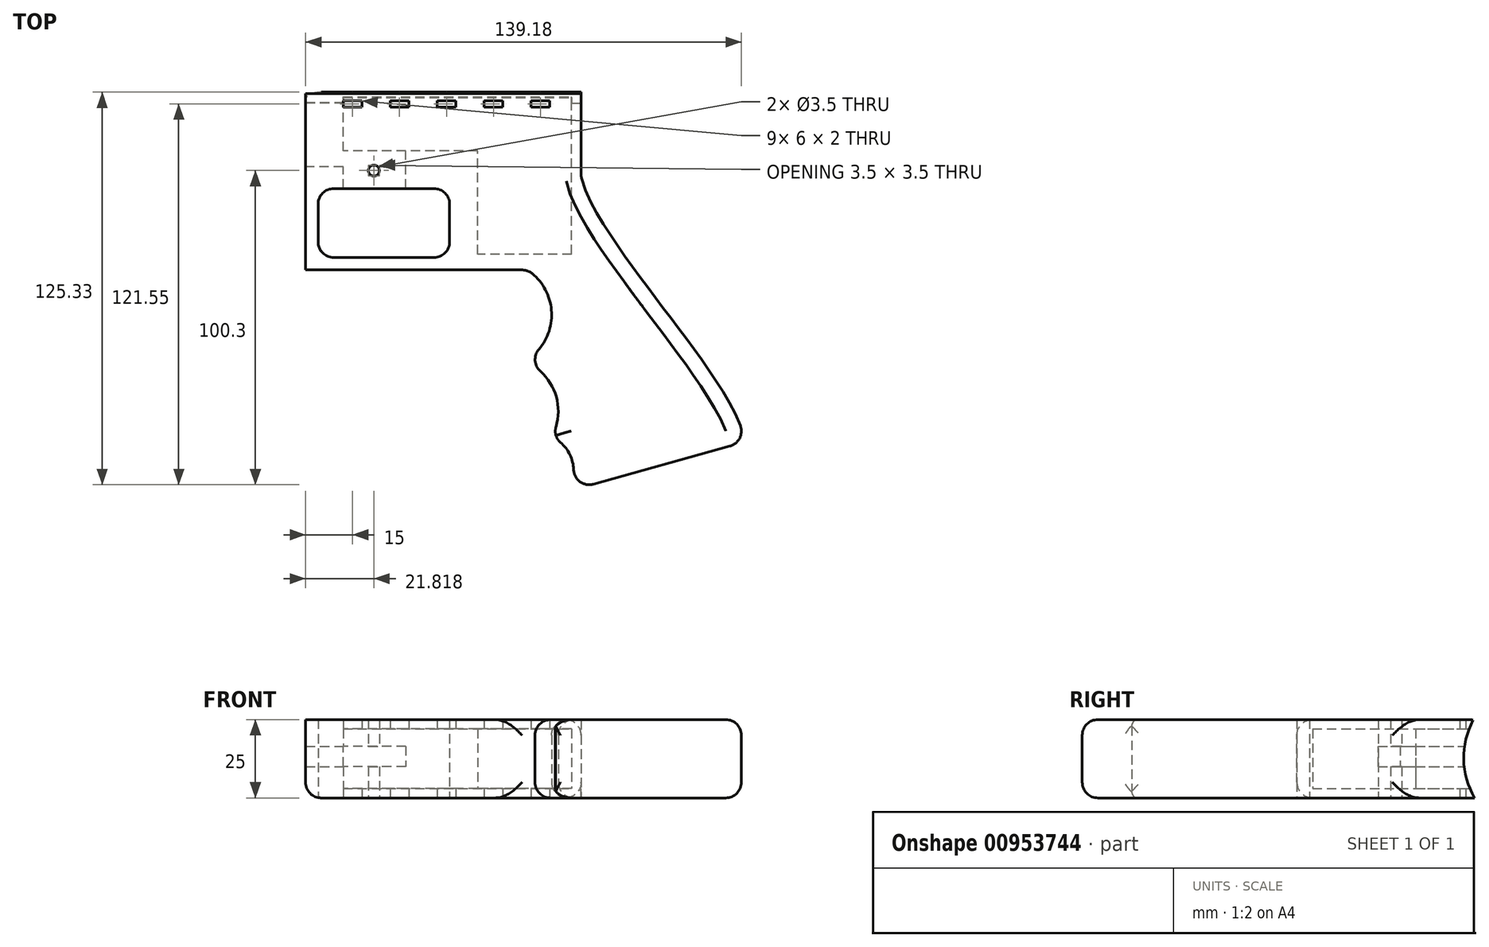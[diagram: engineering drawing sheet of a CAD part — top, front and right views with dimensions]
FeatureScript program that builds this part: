
annotation { "Feature Type Name" : "Feature", "Feature Type Description" : "" }
export const myFeature = defineFeature(function(context is Context, id is Id, definition is map)
    precondition{}
    {
        {
            var Q0;
            Q0=qCreatedBy(makeId("Top.planeOp"),FACE);
            var sketch = newSketch(context, id + "F0", { "sketchPlane" : qUnion([Q0])});
            skLineSegment(sketch, "E0.bottom", {"start": v(44, -30) * mm, "end": v(-44, -30) * mm});
            skLineSegment(sketch, "E0.top", {"start": v(44, 30) * mm, "end": v(-44, 30) * mm});
            skLineSegment(sketch, "E0.left", {"start": v(44, -30) * mm, "end": v(44, 30) * mm});
            skLineSegment(sketch, "E0.right", {"start": v(-44, -30) * mm, "end": v(-44, 30) * mm});
            skPoint(sketch, "E0.middle", {"position": v(0, 0) * mm});
            skLineSegment(sketch, "E1.bottom", {"start": v(-40, -26) * mm, "end": v(2, -26) * mm});
            skLineSegment(sketch, "E1.top", {"start": v(-40, -4) * mm, "end": v(2, -4) * mm});
            skLineSegment(sketch, "E1.left", {"start": v(-40, -26) * mm, "end": v(-40, -4) * mm});
            skLineSegment(sketch, "E1.right", {"start": v(2, -26) * mm, "end": v(2, -4) * mm});
            skLineSegment(sketch, "E2.bottom", {"start": v(-32, 24) * mm, "end": v(-26, 24) * mm});
            skLineSegment(sketch, "E2.top", {"start": v(-32, 22) * mm, "end": v(-26, 22) * mm});
            skLineSegment(sketch, "E2.left", {"start": v(-32, 24) * mm, "end": v(-32, 22) * mm});
            skLineSegment(sketch, "E2.right", {"start": v(-26, 24) * mm, "end": v(-26, 22) * mm});
            skLineSegment(sketch, "E3.1.0.0", {"start": v(-17, 22) * mm, "end": v(-11, 22) * mm});
            skLineSegment(sketch, "E3.1.0.1", {"start": v(-17, 24) * mm, "end": v(-17, 22) * mm});
            skLineSegment(sketch, "E3.1.0.2", {"start": v(-17, 24) * mm, "end": v(-11, 24) * mm});
            skLineSegment(sketch, "E3.1.0.3", {"start": v(-11, 24) * mm, "end": v(-11, 22) * mm});
            skLineSegment(sketch, "E3.2.0.0", {"start": v(-2, 22) * mm, "end": v(4, 22) * mm});
            skLineSegment(sketch, "E3.2.0.1", {"start": v(-2, 24) * mm, "end": v(-2, 22) * mm});
            skLineSegment(sketch, "E3.2.0.2", {"start": v(-2, 24) * mm, "end": v(4, 24) * mm});
            skLineSegment(sketch, "E3.2.0.3", {"start": v(4, 24) * mm, "end": v(4, 22) * mm});
            skLineSegment(sketch, "E3.3.0.0", {"start": v(13, 22) * mm, "end": v(19, 22) * mm});
            skLineSegment(sketch, "E3.3.0.1", {"start": v(13, 24) * mm, "end": v(13, 22) * mm});
            skLineSegment(sketch, "E3.3.0.2", {"start": v(13, 24) * mm, "end": v(19, 24) * mm});
            skLineSegment(sketch, "E3.3.0.3", {"start": v(19, 24) * mm, "end": v(19, 22) * mm});
            skLineSegment(sketch, "E3.4.0.0", {"start": v(28, 22) * mm, "end": v(34, 22) * mm});
            skLineSegment(sketch, "E3.4.0.1", {"start": v(28, 24) * mm, "end": v(28, 22) * mm});
            skLineSegment(sketch, "E3.4.0.2", {"start": v(28, 24) * mm, "end": v(34, 24) * mm});
            skLineSegment(sketch, "E3.4.0.3", {"start": v(34, 24) * mm, "end": v(34, 22) * mm});
            skLineSegment(sketch, "E3.direction1", {"start": v(-32, 22) * mm, "end": v(-17, 22) * mm, "construction": true});
            skPoint(sketch, "E4", {"position": v(44, 0) * mm});
            skFitSpline(sketch, "E5", {"points": [v(44, 0) * mm, v(96, -85) * mm], "startDerivative": vector(11.02, -60.11) * mm, "endDerivative": vector(0.72, -52.1) * mm});
            skLineSegment(sketch, "E6", {"start": v(96, -85) * mm, "end": v(42.05, -100) * mm});
            skLineSegment(sketch, "E7", {"start": v(42.05, -100) * mm, "end": v(41.24, -97.1) * mm});
            skArc(sketch, "E8", {"start": v(41.24, -97.1) * mm, "mid": v(40.82, -89.9) * mm, "end": v(36.33, -84.24) * mm});
            skLineSegment(sketch, "E9", {"start": v(36.33, -84.24) * mm, "end": v(35.52, -81.35) * mm});
            skArc(sketch, "E10", {"start": v(35.52, -81.35) * mm, "mid": v(35.86, -69.78) * mm, "end": v(28.72, -60.68) * mm});
            skLineSegment(sketch, "E11", {"start": v(28.72, -60.68) * mm, "end": v(27.92, -57.8) * mm});
            skArc(sketch, "E12", {"start": v(27.92, -57.8) * mm, "mid": v(34.57, -43.6) * mm, "end": v(26.78, -30) * mm});
            skSolve(sketch);
        }
        {
            var Q0;
            {var subQ4=sQuery(id+"F0.wireOp",EDGE,"E0.top");Q0=makeQuery(id+"F0.imprint","IMPRINT",FACE,{"disambiguationData":[TD([[makeQuery(id+"F0.imprint","IMPRINT",EDGE,{"derivedFrom":subQ4}),1.0]])]});}
            var Q1;
            {var subQ3=sQuery(id+"F0.wireOp",EDGE,"E5");Q1=makeQuery(id+"F0.imprint","IMPRINT",FACE,{"disambiguationData":[TD([[makeQuery(id+"F0.imprint","IMPRINT",EDGE,{"derivedFrom":subQ3}),-1.0]])]});}
            extrude(context, id + "F1", {"entities" : qUnion([Q0, Q1]), "depth" : 25 * mm, "offsetDistance" : 25 * mm});
        }
        {
            var Q0;
            Q0=makeQuery(id+"F1.opExtrude","SWEPT_FACE",FACE,{"disambiguationData":[OSD([sQuery(id+"F0.wireOp",EDGE,"E0.top")])]});
            var sketch = newSketch(context, id + "F2", { "sketchPlane" : qUnion([Q0])});
            skLineSegment(sketch, "E13.bottom", {"start": v(-41, 22) * mm, "end": v(32, 22) * mm});
            skLineSegment(sketch, "E13.top", {"start": v(-41, 3) * mm, "end": v(32, 3) * mm});
            skLineSegment(sketch, "E13.left", {"start": v(-41, 22) * mm, "end": v(-41, 3) * mm});
            skLineSegment(sketch, "E13.right", {"start": v(32, 22) * mm, "end": v(32, 3) * mm});
            skPoint(sketch, "E14", {"position": v(-41, 3) * mm});
            skPoint(sketch, "E15", {"position": v(-41, 22) * mm});
            skPoint(sketch, "E16", {"position": v(32, 3) * mm});
            skLineSegment(sketch, "E17", {"start": v(-11, 22) * mm, "end": v(-11, 3) * mm});
            skLineSegment(sketch, "E18.bottom", {"start": v(12, 16.48) * mm, "end": v(44, 16.48) * mm});
            skLineSegment(sketch, "E18.top", {"start": v(12, 9.98) * mm, "end": v(44, 9.98) * mm});
            skLineSegment(sketch, "E18.left", {"start": v(12, 16.48) * mm, "end": v(12, 9.98) * mm});
            skLineSegment(sketch, "E18.right", {"start": v(44, 16.48) * mm, "end": v(44, 9.98) * mm});
            skSolve(sketch);
        }
        {
            var Q0;
            Q0 = qSketchRegion(id + "F2", true);
            extrude(context, id + "F3", {"entities" : qUnion([Q0]), "operationType" : NewBodyOperationType.REMOVE, "oppositeDirection" : true, "depth" : 22 * mm, "offsetDistance" : 25 * mm});
        }
        {
            var Q0;
            {var subQ0=sQuery(id+"F2.wireOp",EDGE,"E13.left");Q0=makeQuery(id+"F2.imprint","IMPRINT",FACE,{"disambiguationData":[TD([[makeQuery(id+"F2.imprint","IMPRINT",EDGE,{"derivedFrom":subQ0}),1.0]])]});}
            extrude(context, id + "F4", {"entities" : qUnion([Q0]), "operationType" : NewBodyOperationType.REMOVE, "oppositeDirection" : true, "depth" : 55 * mm, "offsetDistance" : 25 * mm});
        }
        {
            var Q0;
            {var subQ5=sQuery(id+"F2.wireOp",EDGE,"E18.left");Q0=makeQuery(id+"F2.imprint","IMPRINT",FACE,{"disambiguationData":[TD([[makeQuery(id+"F2.imprint","IMPRINT",EDGE,{"derivedFrom":subQ5}),1.0]])]});}
            var Q1;
            Q1=makeQuery(id+"F1.opExtrude","SWEPT_FACE",FACE,{"disambiguationData":[OSD([sQuery(id+"F0.wireOp",EDGE,"E1.top")])]});
            extrude(context, id + "F5", {"entities" : qUnion([Q0]), "operationType" : NewBodyOperationType.REMOVE, "endBound" : BoundingType.UP_TO_SURFACE, "oppositeDirection" : true, "depth" : 25 * mm, "endBoundEntityFace" : qUnion([Q1]), "offsetDistance" : 25 * mm});
        }
        {
            var Q0;
            {var subQ5=sQuery(id+"F2.wireOp",EDGE,"E18.right");Q0=makeQuery(id+"F2.imprint","IMPRINT",FACE,{"disambiguationData":[TD([[makeQuery(id+"F2.imprint","IMPRINT",EDGE,{"derivedFrom":subQ5}),-1.0]])]});}
            extrude(context, id + "F6", {"entities" : qUnion([Q0]), "operationType" : NewBodyOperationType.REMOVE, "oppositeDirection" : true, "depth" : 27 * mm, "offsetDistance" : 25 * mm});
        }
        {
            var Q0;
            Q0=makeQuery(id+"F1.opExtrude","SWEPT_FACE",FACE,{"disambiguationData":[OSD([sQuery(id+"F0.wireOp",EDGE,"E12")])]});
            fillet(context, id + "F7", {"entities" : qUnion([Q0]), "radius" : 5 * mm, "tangentPropagation" : true, "allowEdgeOverflow" : false});
        }
        {
            var Q0;
            Q0=makeQuery(id+"F1.opExtrude","SWEPT_FACE",FACE,{"disambiguationData":[OSD([sQuery(id+"F0.wireOp",EDGE,"E10")])]});
            var Q1;
            Q1=makeQuery(id+"F1.opExtrude","SWEPT_FACE",FACE,{"disambiguationData":[OSD([sQuery(id+"F0.wireOp",EDGE,"E8")])]});
            fillet(context, id + "F8", {"entities" : qUnion([Q0, Q1]), "radius" : 5 * mm, "tangentPropagation" : true, "allowEdgeOverflow" : false});
        }
        {
            var Q0;
            Q0=makeQuery(id+"F1.opExtrude","SWEPT_FACE",FACE,{"disambiguationData":[OSD([sQuery(id+"F0.wireOp",EDGE,"E5")])]});
            var Q1;
            Q1=makeQuery(id+"F1.opExtrude","SWEPT_FACE",FACE,{"disambiguationData":[OSD([sQuery(id+"F0.wireOp",EDGE,"E6")])]});
            var Q2;
            Q2=makeQuery(id+"F1.opExtrude","SWEPT_EDGE",EDGE,{"disambiguationData":[OSD([sQuery(id+"F0.wireOp",EDGE,"E1.top"),sQuery(id+"F0.wireOp",EDGE,"E1.right")])]});
            var Q3;
            Q3=makeQuery(id+"F1.opExtrude","SWEPT_EDGE",EDGE,{"disambiguationData":[OSD([sQuery(id+"F0.wireOp",EDGE,"E1.bottom"),sQuery(id+"F0.wireOp",EDGE,"E1.right")])]});
            var Q4;
            Q4=makeQuery(id+"F1.opExtrude","SWEPT_EDGE",EDGE,{"disambiguationData":[OSD([sQuery(id+"F0.wireOp",EDGE,"E1.top"),sQuery(id+"F0.wireOp",EDGE,"E1.left")])]});
            var Q5;
            Q5=makeQuery(id+"F1.opExtrude","SWEPT_EDGE",EDGE,{"disambiguationData":[OSD([sQuery(id+"F0.wireOp",EDGE,"E1.bottom"),sQuery(id+"F0.wireOp",EDGE,"E1.left")])]});
            fillet(context, id + "F9", {"entities" : qUnion([Q0, Q1, Q2, Q3, Q4, Q5]), "radius" : 5 * mm, "tangentPropagation" : true, "allowEdgeOverflow" : false});
        }
        {
            var Q0;
            Q0=makeQuery(id+"F1.opExtrude","CAP_EDGE",EDGE,{"disambiguationData":[OSD([sQuery(id+"F0.wireOp",EDGE,"E0.right")])],"isStart":true});
            var Q1;
            Q1=makeQuery(id+"F1.opExtrude","CAP_EDGE",EDGE,{"disambiguationData":[OSD([sQuery(id+"F0.wireOp",EDGE,"E0.top")])],"isStart":false});
            fillet(context, id + "F10", {"entities" : qUnion([Q0, Q1]), "radius" : 5 * mm, "tangentPropagation" : true, "allowEdgeOverflow" : false});
        }
        {
            var Q0;
            Q0=qCreatedBy(makeId("Top.planeOp"),FACE);
            var sketch = newSketch(context, id + "F11", { "sketchPlane" : qUnion([Q0])});
            skCircle(sketch, "E19", {"center": v(-22.18, 1.75) * mm, "radius": 1.75 * mm});
            skSolve(sketch);
        }
        {
            var Q0;
            Q0 = qSketchRegion(id + "F11", true);
            extrude(context, id + "F12", {"entities" : qUnion([Q0]), "operationType" : NewBodyOperationType.REMOVE, "depth" : 25 * mm, "offsetDistance" : 25 * mm});
        }
        {
            var Q0;
            Q0=makeQuery(id+"F1.opExtrude","SWEPT_FACE",FACE,{"disambiguationData":[OSD([sQuery(id+"F0.wireOp",EDGE,"E0.left")])]});
            var sketch = newSketch(context, id + "F13", { "sketchPlane" : qUnion([Q0])});
            skPoint(sketch, "E20.first.point", {"position": v(-35.12, 52.23) * mm});
            skPoint(sketch, "E20.second.point", {"position": v(-60.86, 43.97) * mm});
            skPoint(sketch, "E20.third.point", {"position": v(-32.61, 38.73) * mm});
            skCircle(sketch, "E21", {"center": v(48.69, 12.85) * mm, "radius": 25.4 * mm});
            skSolve(sketch);
        }
        {
            var Q0;
            {var subQ0=sQuery(id+"F13.wireOp",EDGE,"E21");var subQ1=makeQuery(id+"F10.opFillet","BLEND_EDGE",EDGE,{"blendedFrom":[makeQuery(id+"F1.opExtrude","CAP_EDGE",EDGE,{"disambiguationData":[OSD([sQuery(id+"F0.wireOp",EDGE,"E0.top")])],"isStart":true}),makeQuery(id+"F1.opExtrude","SWEPT_FACE",FACE,{"disambiguationData":[OSD([sQuery(id+"F0.wireOp",EDGE,"E0.left")])]})],"blendedInto":[makeQuery(id+"F1.opExtrude","SWEPT_FACE",FACE,{"disambiguationData":[OSD([sQuery(id+"F0.wireOp",EDGE,"E0.left")])]})]});var subQ2=makeQuery(id+"F13.imprint","INTERSECT",VERTEX,{"disambiguationData":[OD(0.0)],"derivedFrom":[subQ1,subQ0]});Q0=makeQuery(id+"F13.imprint","IMPRINT",FACE,{"disambiguationData":[TD([[makeQuery(id+"F13.imprint","IMPRINT",EDGE,{"disambiguationData":[TD([[subQ2,-1.0]])],"derivedFrom":subQ0}),1.0]])]});}
            extrude(context, id + "F14", {"entities" : qUnion([Q0]), "operationType" : NewBodyOperationType.REMOVE, "oppositeDirection" : true, "depth" : 200 * mm, "offsetDistance" : 25 * mm});
        }
    });
